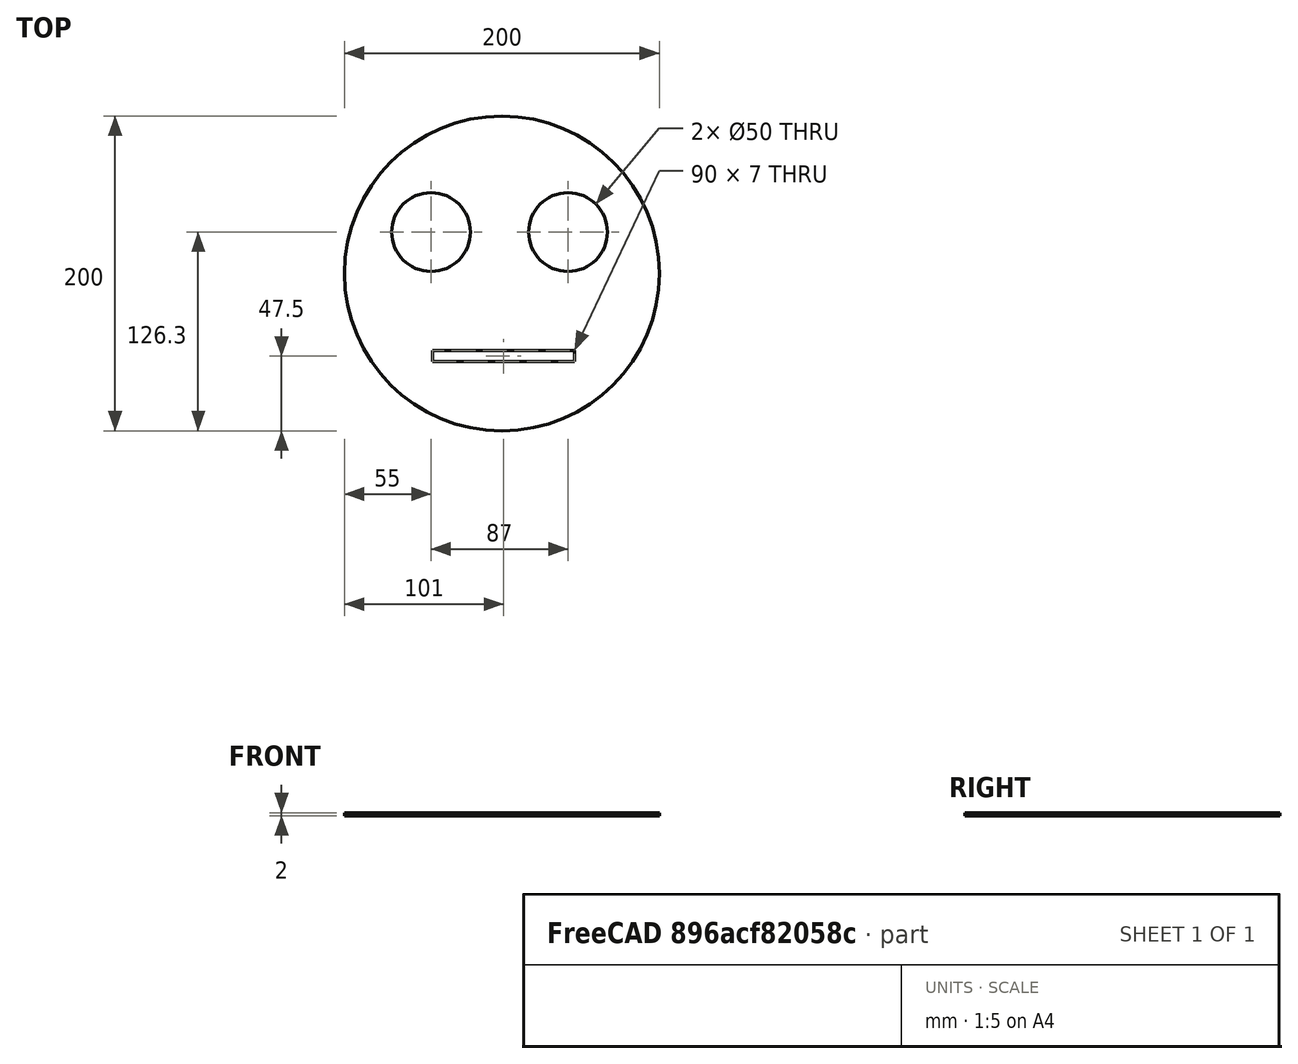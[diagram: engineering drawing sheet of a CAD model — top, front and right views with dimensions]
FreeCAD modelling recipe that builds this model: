
FCSTD DOCUMENT  (FreeCAD 0.18R16117 (Git))
Label: mocksmile
License: All rights reserved
LicenseURL: http://en.wikipedia.org/wiki/All_rights_reserved
objects: Part::Cylinder×3, Part::Cut×3, Part::Box×1
note: 7 computed .brp shape members not serialized (recipe doc carries the construction recipe); baked Part::Feature solids carry a one-line shape summary decoded from their .brp

FEATURE [Part::Cylinder] Cylinder
  Angle = 360
  AttacherType = Attacher::AttachEngine3D
  Height = 2
  Radius = 100
FEATURE [Part::Cylinder] Cylinder001
  Angle = 360
  AttacherType = Attacher::AttachEngine3D
  Height = 2
  Placement = pos=(-45,26.3,0) rot=(0,0,1;0rad)
  Radius = 25
FEATURE [Part::Box] Box  label="Cube"
  AttacherType = Attacher::AttachEngine3D
  Height = 2
  Length = 90
  Placement = pos=(-44,-56,0) rot=(0,0,1;0rad)
  Width = 7
FEATURE [Part::Cylinder] Cylinder002
  Angle = 360
  AttacherType = Attacher::AttachEngine3D
  Height = 2
  Placement = pos=(42,26.3,0) rot=(0,0,1;0rad)
  Radius = 25
FEATURE [Part::Cut] Cut
  Base = -> Cylinder
  Tool = -> Box
FEATURE [Part::Cut] Cut001
  Base = -> Cut
  Tool = -> Cylinder001
FEATURE [Part::Cut] Cut002
  Base = -> Cut001
  Tool = -> Cylinder002
